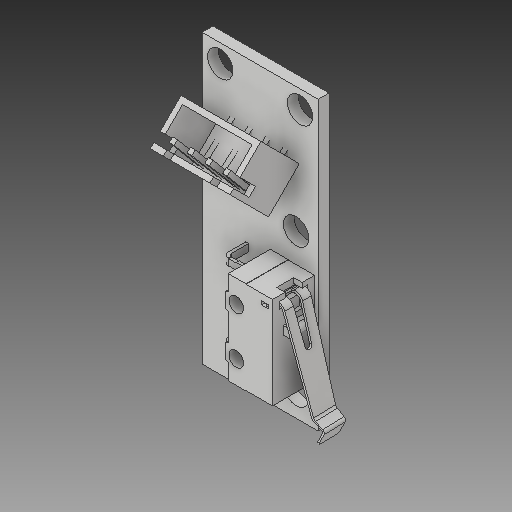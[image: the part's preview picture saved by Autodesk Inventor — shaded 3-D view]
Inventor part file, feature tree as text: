
AUTODESK INVENTOR PART (.ipt)
format: ipt  version: 2018 (Build 220112000, 112)  size: 378,880 bytes
history: native  units: mm
features: other x12, revolve x2, direct_edit x1, move_body x1
ambient origin geometry x8: Origin, YZ Plane, XZ Plane, XY Plane, X Axis, Y Axis, Z Axis, Center Point
bodies: Solid1 (feature_tree), Solid2 (feature_tree), Solid3 (feature_tree), Solid4 (feature_tree), Solid5 (feature_tree), Solid6 (feature_tree), Solid7 (feature_tree), Solid8 (feature_tree), Solid9 (feature_tree), Solid10 (feature_tree), Solid11 (feature_tree), Solid12 (feature_tree)
feature tree (16):
  direct_edit  "Direct Edit1"
  other  "Embase alim end stop.1:1"
  other  "Embase alim end stop.1:2"
  other  "Embase alim end stop.1:3"
  other  "Embase alim end stop.1:4"
  other  "Embase alim end stop.1:5"
  other  "Boitier plastique:1"
  other  "Bouton:1"
  other  "Levier:1"
  other  "Contact:1"
  other  "Contact 2:1"
  other  "Contact 3:1"
  other  "Pièce1.1:1"
  revolve  "Rotate1"  Angle=45.0deg
  move_body  "Move1"
  revolve  "Rotate2"  [1 undecoded]
note: 1 required parameter value undecoded (feature->parameter linkage not recoverable at this tier; creation-order binding heuristic only, values carry confidence <= 0.55)
